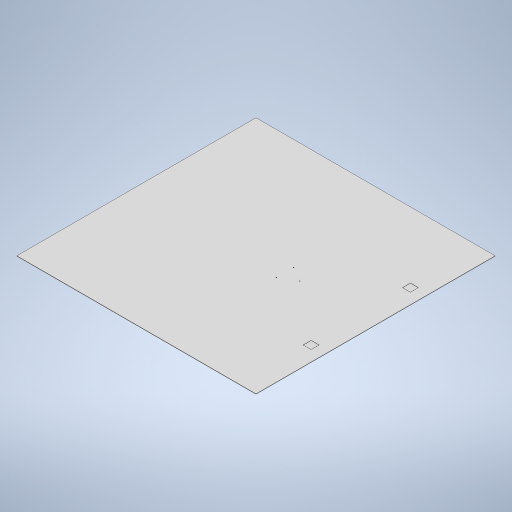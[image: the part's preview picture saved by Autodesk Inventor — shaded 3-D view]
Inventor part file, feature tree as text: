
AUTODESK INVENTOR PART (.ipt)
format: ipt  version: 2024 (Build 280153000, 153)  size: 259,584 bytes
history: native  units: mm
features: extrude x3, sketch x3, other x1
ambient origin geometry x8: Origin, YZ Plane, XZ Plane, XY Plane, X Axis, Y Axis, Z Axis, Center Point
bodies: Body1 (feature_tree)
feature tree (7):
  other  "Sólido1"
  extrude  "Extrusión1"  Depth=6000.0mm
  extrude  "Extrusión2"  Depth=10.0mm
  extrude  "Extrusión3"  Depth=4.0mm
  sketch  "Boceto1"  dims[d0=6000.0mm d1=6000.0mm]
  sketch  "Boceto2"  dims[d2=10.0mm d3=0.0mm d4=18.5mm]
  sketch  "Boceto3"  dims[d5=1900.0mm d6=18.5mm d7=375.0mm d8=18.5mm d9=18.5mm d10=216.5mm d12=10.0mm d13=0.0mm d14=375.0mm d15=200.0mm d16=200.0mm d17=200.0mm d18=2691.9936mm d19=1345.997mm d21=1630.0mm d22=4.0mm d23=0.0mm]
